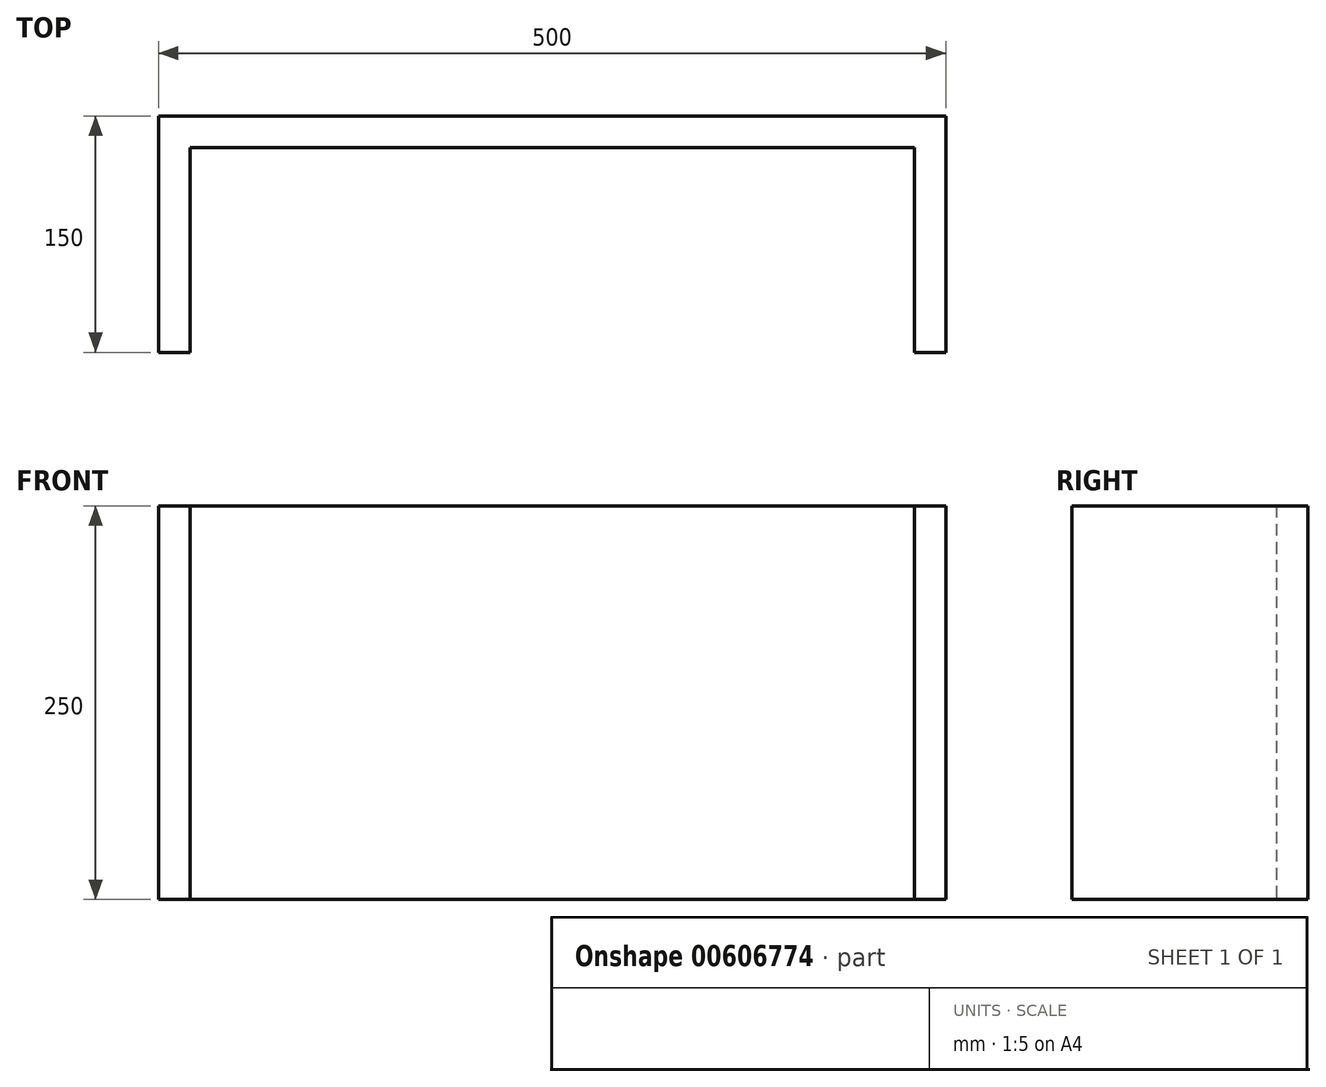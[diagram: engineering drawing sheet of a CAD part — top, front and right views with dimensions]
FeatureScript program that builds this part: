
annotation { "Feature Type Name" : "Feature", "Feature Type Description" : "" }
export const myFeature = defineFeature(function(context is Context, id is Id, definition is map)
    precondition{}
    {
        {
            var Q0;
            Q0=qCreatedBy(makeId("Top.planeOp"),FACE);
            var sketch = newSketch(context, id + "F0", { "sketchPlane" : qUnion([Q0])});
            skLineSegment(sketch, "E0", {"start": v(0, 150) * mm, "end": v(250, 150) * mm});
            skLineSegment(sketch, "E1", {"start": v(250, 150) * mm, "end": v(250, 0) * mm});
            skLineSegment(sketch, "E2", {"start": v(250, 0) * mm, "end": v(230, 0) * mm});
            skLineSegment(sketch, "E3", {"start": v(0, 130) * mm, "end": v(230, 130) * mm});
            skLineSegment(sketch, "E4", {"start": v(230, 130) * mm, "end": v(230, 0) * mm});
            skLineSegment(sketch, "E5.MirrorCS", {"start": v(0, 150) * mm, "end": v(-250, 150) * mm});
            skLineSegment(sketch, "E6.MirrorCS", {"start": v(0, 130) * mm, "end": v(-230, 130) * mm});
            skLineSegment(sketch, "E7.MirrorCS", {"start": v(-230, 130) * mm, "end": v(-230, 0) * mm});
            skLineSegment(sketch, "E8.MirrorCS", {"start": v(-250, 150) * mm, "end": v(-250, 0) * mm});
            skLineSegment(sketch, "E9.MirrorCS", {"start": v(-250, 0) * mm, "end": v(-230, 0) * mm});
            skPoint(sketch, "E10.orphan", {"position": v(0, 0) * mm});
            skSolve(sketch);
        }
        {
            var Q0;
            Q0=makeQuery(id+"F0.imprint","IMPRINT",FACE,{"disambiguationData":[TD([[makeQuery(id+"F0.imprint","IMPRINT",EDGE,{"derivedFrom":sQuery(id+"F0.wireOp",EDGE,"E0")}),-1.0]])]});
            extrude(context, id + "F1", {"entities" : qUnion([Q0]), "depth" : 250 * mm, "offsetDistance" : 25 * mm});
        }
    });
